# Revit family: Domotics-DomesticRanges-GEWISS-CHORUS_COMMAND-TOUCH_MODULE
name_source: partatom
category: Apparecchi elettrici
revit_build: Autodesk Revit 2016 (Build: 20161004_0715(x64)
units: mm (PartAtom-declared; Revit-internal decimal feet)

## family parameters
Condiviso = Sì
Host = Superficie
Mantenere orientamento annotazione = Sì
Numero OmniClass = 23.80.50.11.14
Punto di calcolo locali = No
Quota connettore circolare = Usa diametro
Taglio con vuoti quando caricato = Sì
Tipo di parte = Normale
Titolo OmniClass = Switches

## types (3) — shared parameters
Catalogue = DOMOTICS
Catalogue Range = CHORUS - DOMESTIC RANGE
Command = Touch
Control = Touch
Electrocod = 0141
IDF = 12b0142f-1a5b-4151-9d34-bc9901184afe
IDT = ac854c82-4ccb-49c1-816b-b33916bdc0f6
Immagine tipo = GW10909.jpg
Larghezza pulsante = 23 mm  [stored 0.0754593 ft]
No. Chorus modules = 1
No. Chorus modules: = 1
Produttore = GEWISS S.p.A.
Prospetto di default = 1219 mm
Simbolo = SIMBOLO COMANDI TOUCH : RIPETITORE
Supply voltage = 230V ac - 50 Hz
Technical sheet = https://www.gewiss.com
Tipo = CHORUS MODULI COMANDI TOUCH_BASE : GW10909 - Bianco
URL = https://www.gewiss.com
Version file RFA = 19.0
Voltage = 230V ac - 50 Hz

## per-type parameters (varying)
| type | Description. | Descrizione | EAN code | Inductive load | Modello | Resistive load | SEO |
| GW10908 - White | Dimmers | TOUCH DIMMER MODULE 1M WHITE | 8011564759930 | 40 - 300 VA | GW10908 | 40 - 300 W | Dimmer |
| GW10907 - White | Switch | TOUCH ONE-WAY SWITCH MODULE 1M WHITE | 8011564759879 |  | GW10907 |  | 1 way switch |
| GW10909 - White | Command repeater | TOUCH COMMAND DUPLICATOR MODULE 1M WHITE | 8011564759886 |  | GW10909 |  | Duplicator |

note: [stored X ft] marks values corroborated as IEEE doubles in the binary element streams (Revit-internal decimal feet)

## geometry (parser evidence)
native form markers: Sweep x1
no freeform markers — native parametric forms only
